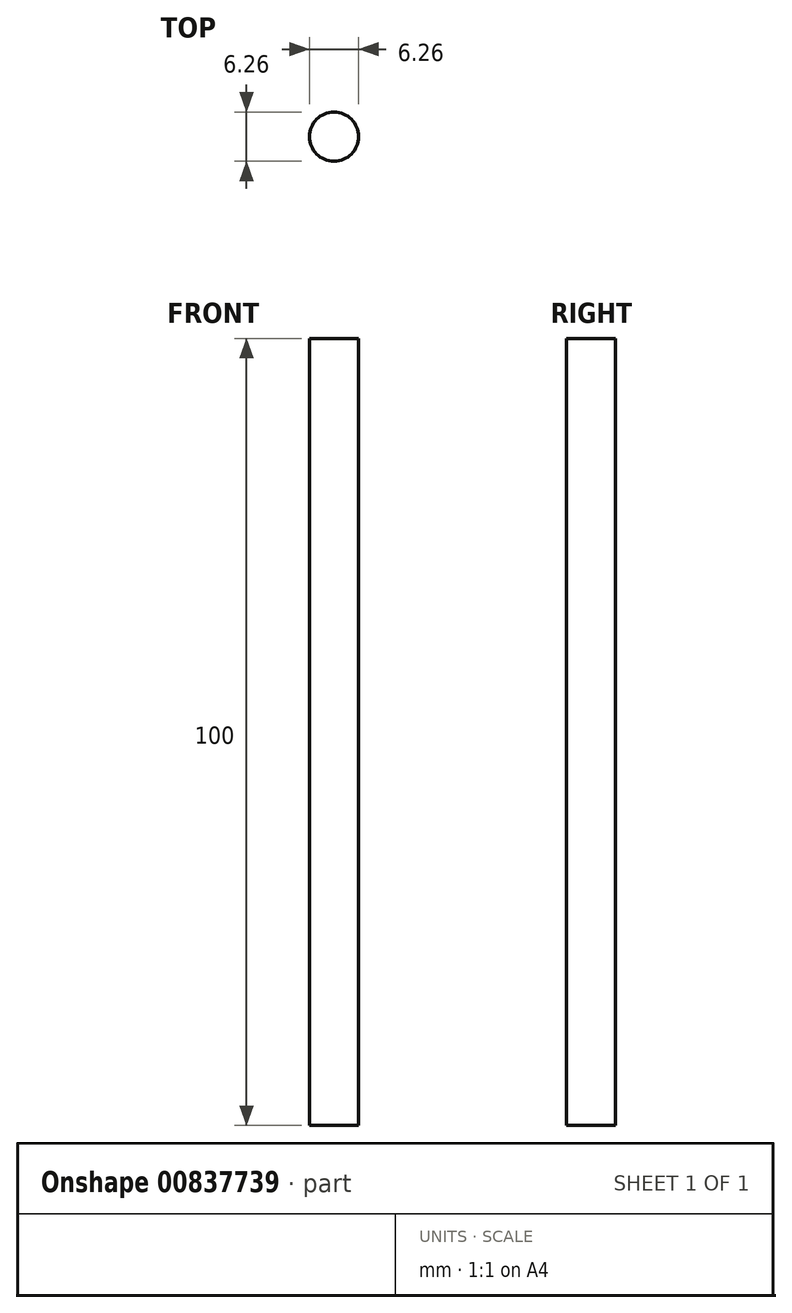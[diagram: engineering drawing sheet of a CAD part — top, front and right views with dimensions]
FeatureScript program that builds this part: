
annotation { "Feature Type Name" : "Feature", "Feature Type Description" : "" }
export const myFeature = defineFeature(function(context is Context, id is Id, definition is map)
    precondition{}
    {
        {
            var Q0;
            Q0=qCreatedBy(makeId("Top.planeOp"),FACE);
            var sketch = newSketch(context, id + "F0", { "sketchPlane" : qUnion([Q0])});
            skCircle(sketch, "E0", {"center": v(0, 0) * mm, "radius": 3.12 * mm});
            skSolve(sketch);
        }
        {
            var Q0;
            Q0=makeQuery(id+"F0.imprint","IMPRINT",FACE,{"disambiguationData":[TD([[makeQuery(id+"F0.imprint","IMPRINT",EDGE,{"derivedFrom":sQuery(id+"F0.wireOp",EDGE,"E0")}),1.0]])]});
            extrude(context, id + "F1", {"entities" : qUnion([Q0]), "depth" : 100 * mm, "offsetDistance" : 25 * mm});
        }
    });
